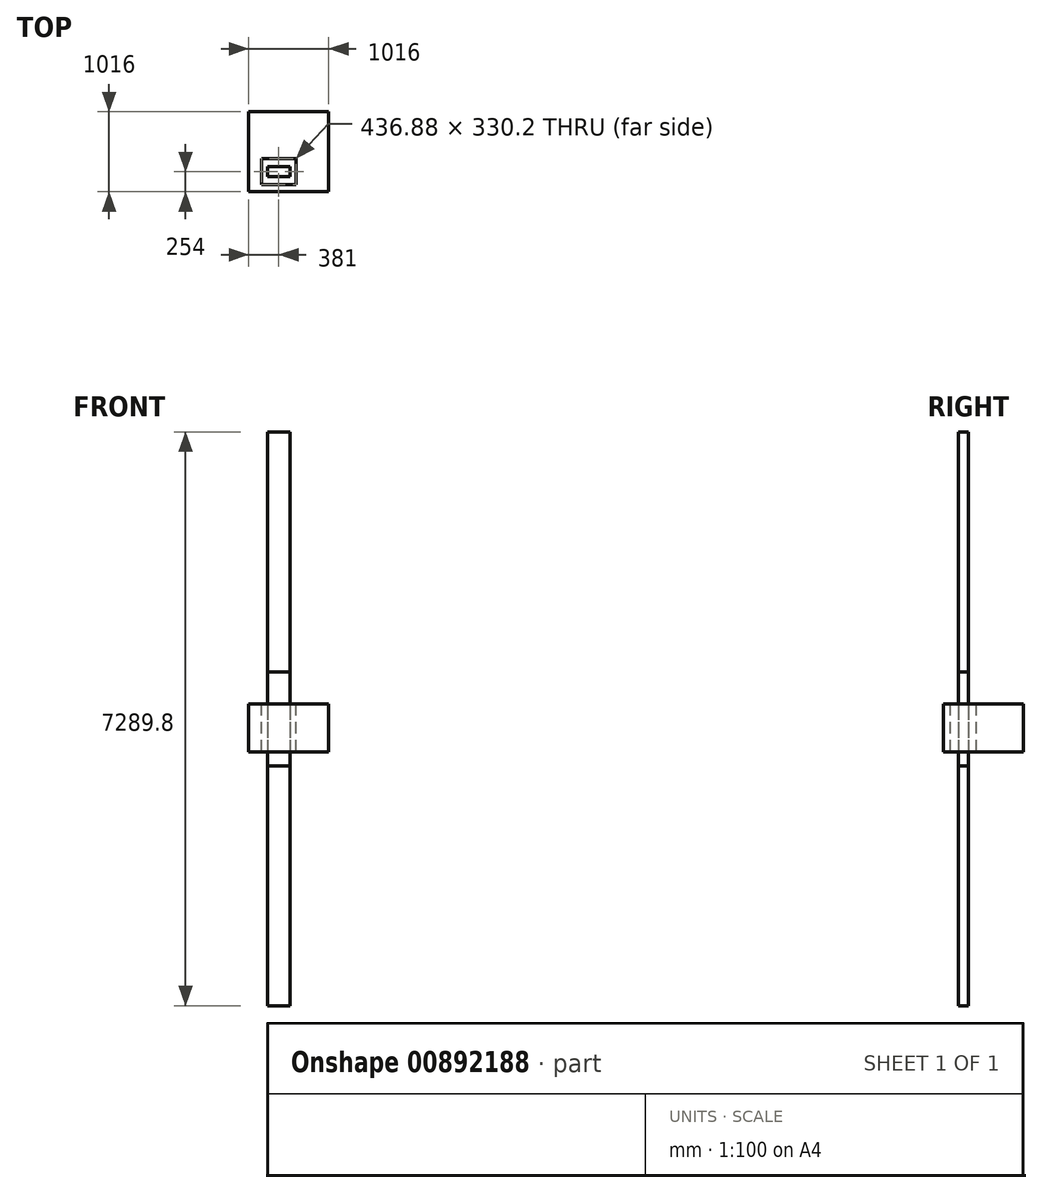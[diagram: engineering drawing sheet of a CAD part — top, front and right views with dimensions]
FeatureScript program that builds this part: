
annotation { "Feature Type Name" : "Feature", "Feature Type Description" : "" }
export const myFeature = defineFeature(function(context is Context, id is Id, definition is map)
    precondition{}
    {
        {
            var Q0;
            Q0=qCreatedBy(makeId("Top.planeOp"),FACE);
            var sketch = newSketch(context, id + "F0", { "sketchPlane" : qUnion([Q0])});
            skLineSegment(sketch, "E0.bottom", {"start": v(0, 0) * mm, "end": v(1016, 0) * mm});
            skLineSegment(sketch, "E0.top", {"start": v(0, 1016) * mm, "end": v(1016, 1016) * mm});
            skLineSegment(sketch, "E0.left", {"start": v(0, 0) * mm, "end": v(0, 1016) * mm});
            skLineSegment(sketch, "E0.right", {"start": v(1016, 0) * mm, "end": v(1016, 1016) * mm});
            skSolve(sketch);
        }
        {
            var Q0;
            Q0=makeQuery(id+"F0.imprint","IMPRINT",FACE,{"disambiguationData":[TD([[makeQuery(id+"F0.imprint","IMPRINT",EDGE,{"derivedFrom":sQuery(id+"F0.wireOp",EDGE,"E0.bottom")}),1.0]])]});
            extrude(context, id + "F1", {"entities" : qUnion([Q0]), "depth" : 609.6 * mm, "offsetDistance" : 25.4 * mm});
        }
        {
            var Q0;
            Q0=makeQuery(id+"F1.opExtrude","CAP_FACE",FACE,{"disambiguationData":[OSD([sQuery(id+"F0.wireOp",EDGE,"E0.bottom"),sQuery(id+"F0.wireOp",EDGE,"E0.top"),sQuery(id+"F0.wireOp",EDGE,"E0.left"),sQuery(id+"F0.wireOp",EDGE,"E0.right")])],"isStart":false});
            var sketch = newSketch(context, id + "F2", { "sketchPlane" : qUnion([Q0])});
            skLineSegment(sketch, "E1.bottom", {"start": v(0, 0) * mm, "end": v(381, 0) * mm, "construction": true});
            skLineSegment(sketch, "E1.top", {"start": v(0, 254) * mm, "end": v(381, 254) * mm, "construction": true});
            skLineSegment(sketch, "E1.left", {"start": v(0, 0) * mm, "end": v(0, 254) * mm, "construction": true});
            skLineSegment(sketch, "E1.right", {"start": v(381, 0) * mm, "end": v(381, 254) * mm, "construction": true});
            skLineSegment(sketch, "E2.bottom", {"start": v(523.24, 317.5) * mm, "end": v(238.76, 317.5) * mm});
            skLineSegment(sketch, "E2.top", {"start": v(523.24, 190.5) * mm, "end": v(238.76, 190.5) * mm});
            skLineSegment(sketch, "E2.left", {"start": v(523.24, 317.5) * mm, "end": v(523.24, 190.5) * mm});
            skLineSegment(sketch, "E2.right", {"start": v(238.76, 317.5) * mm, "end": v(238.76, 190.5) * mm});
            skPoint(sketch, "E2.middle", {"position": v(381, 254) * mm});
            skLineSegment(sketch, "E3.bottom", {"start": v(599.44, 419.1) * mm, "end": v(162.56, 419.1) * mm});
            skLineSegment(sketch, "E3.top", {"start": v(599.44, 88.9) * mm, "end": v(162.56, 88.9) * mm});
            skLineSegment(sketch, "E3.left", {"start": v(599.44, 419.1) * mm, "end": v(599.44, 88.9) * mm});
            skLineSegment(sketch, "E3.right", {"start": v(162.56, 419.1) * mm, "end": v(162.56, 88.9) * mm});
            skSolve(sketch);
        }
        {
            var Q0;
            Q0=makeQuery(id+"F2.imprint","IMPRINT",FACE,{"disambiguationData":[TD([[makeQuery(id+"F2.imprint","IMPRINT",EDGE,{"derivedFrom":sQuery(id+"F2.wireOp",EDGE,"E2.bottom")}),-1.0]])]});
            var Q1;
            Q1=makeQuery(id+"F2.imprint","IMPRINT",FACE,{"disambiguationData":[TD([[makeQuery(id+"F2.imprint","IMPRINT",EDGE,{"derivedFrom":sQuery(id+"F2.wireOp",EDGE,"E2.bottom")}),1.0]])]});
            extrude(context, id + "F3", {"entities" : qUnion([Q0, Q1]), "operationType" : NewBodyOperationType.REMOVE, "endBound" : BoundingType.THROUGH_ALL, "oppositeDirection" : true, "depth" : 25.4 * mm, "offsetDistance" : 25.4 * mm});
        }
        {
            var Q0;
            Q0=makeQuery(id+"F2.imprint","IMPRINT",FACE,{"disambiguationData":[TD([[makeQuery(id+"F2.imprint","IMPRINT",EDGE,{"derivedFrom":sQuery(id+"F2.wireOp",EDGE,"E2.bottom")}),1.0]])]});
            extrude(context, id + "F4", {"entities" : qUnion([Q0]), "endBound" : BoundingType.SYMMETRIC, "depth" : 1524 * mm, "offsetDistance" : 25.4 * mm});
        }
        {
            var Q0;
            Q0=makeQuery(id+"F4.opExtrude","CAP_FACE",FACE,{"disambiguationData":[OSD([sQuery(id+"F2.wireOp",EDGE,"E2.bottom"),sQuery(id+"F2.wireOp",EDGE,"E2.top"),sQuery(id+"F2.wireOp",EDGE,"E2.left"),sQuery(id+"F2.wireOp",EDGE,"E2.right")])],"isStart":true});
            extrude(context, id + "F5", {"entities" : qUnion([Q0]), "operationType" : NewBodyOperationType.ADD, "depth" : 1168.4 * mm, "offsetDistance" : 25.4 * mm});
        }
        {
            var Q0;
            Q0=makeQuery(id+"F4.opExtrude","CAP_FACE",FACE,{"disambiguationData":[OSD([sQuery(id+"F2.wireOp",EDGE,"E2.bottom"),sQuery(id+"F2.wireOp",EDGE,"E2.top"),sQuery(id+"F2.wireOp",EDGE,"E2.left"),sQuery(id+"F2.wireOp",EDGE,"E2.right")])],"isStart":false});
            extrude(context, id + "F6", {"entities" : qUnion([Q0]), "operationType" : NewBodyOperationType.ADD, "depth" : 431.8 * mm, "offsetDistance" : 25.4 * mm});
        }
        {
            var Q0;
            Q0=makeQuery(id+"F6.opExtrude","CAP_FACE",FACE,{"disambiguationData":[OSD([sQuery(id+"F2.wireOp",EDGE,"E2.bottom"),sQuery(id+"F2.wireOp",EDGE,"E2.top"),sQuery(id+"F2.wireOp",EDGE,"E2.left"),sQuery(id+"F2.wireOp",EDGE,"E2.right")])],"isStart":false});
            var Q1;
            Q1=makeQuery(id+"F1.opExtrude","CAP_FACE",FACE,{"disambiguationData":[OSD([sQuery(id+"F0.wireOp",EDGE,"E0.bottom"),sQuery(id+"F0.wireOp",EDGE,"E0.top"),sQuery(id+"F0.wireOp",EDGE,"E0.left"),sQuery(id+"F0.wireOp",EDGE,"E0.right")])],"isStart":false});
            extrude(context, id + "F7", {"entities" : qUnion([Q0]), "operationType" : NewBodyOperationType.REMOVE, "endBound" : BoundingType.UP_TO_SURFACE, "oppositeDirection" : true, "depth" : 25.4 * mm, "endBoundEntityFace" : qUnion([Q1]), "offsetDistance" : 25.4 * mm});
        }
        {
            var Q0;
            Q0=makeQuery(id+"F7.boolean.opBoolean","COPY",FACE,{"derivedFrom":makeQuery(id+"F7.opExtrude","CAP_FACE",FACE,{"disambiguationData":[OSD([sQuery(id+"F2.wireOp",EDGE,"E2.bottom"),sQuery(id+"F2.wireOp",EDGE,"E2.top"),sQuery(id+"F2.wireOp",EDGE,"E2.left"),sQuery(id+"F2.wireOp",EDGE,"E2.right")])],"isStart":false})});
            extrude(context, id + "F8", {"entities" : qUnion([Q0]), "operationType" : NewBodyOperationType.ADD, "depth" : 406.4 * mm, "offsetDistance" : 25.4 * mm});
        }
        {
            var Q0;
            Q0=makeQuery(id+"F5.opExtrude","CAP_FACE",FACE,{"disambiguationData":[OSD([sQuery(id+"F2.wireOp",EDGE,"E2.bottom"),sQuery(id+"F2.wireOp",EDGE,"E2.top"),sQuery(id+"F2.wireOp",EDGE,"E2.left"),sQuery(id+"F2.wireOp",EDGE,"E2.right")])],"isStart":false});
            var Q1;
            Q1=makeQuery(id+"F1.opExtrude","CAP_FACE",FACE,{"disambiguationData":[OSD([sQuery(id+"F0.wireOp",EDGE,"E0.bottom"),sQuery(id+"F0.wireOp",EDGE,"E0.top"),sQuery(id+"F0.wireOp",EDGE,"E0.left"),sQuery(id+"F0.wireOp",EDGE,"E0.right")])],"isStart":true});
            extrude(context, id + "F9", {"entities" : qUnion([Q0]), "operationType" : NewBodyOperationType.REMOVE, "endBound" : BoundingType.UP_TO_SURFACE, "oppositeDirection" : true, "depth" : 25.4 * mm, "endBoundEntityFace" : qUnion([Q1]), "offsetDistance" : 25.4 * mm});
        }
        {
            var Q0;
            Q0=makeQuery(id+"F9.boolean.opBoolean","COPY",FACE,{"derivedFrom":makeQuery(id+"F9.opExtrude","CAP_FACE",FACE,{"disambiguationData":[OSD([sQuery(id+"F2.wireOp",EDGE,"E2.bottom"),sQuery(id+"F2.wireOp",EDGE,"E2.top"),sQuery(id+"F2.wireOp",EDGE,"E2.left"),sQuery(id+"F2.wireOp",EDGE,"E2.right")])],"isStart":false})});
            extrude(context, id + "F10", {"entities" : qUnion([Q0]), "operationType" : NewBodyOperationType.ADD, "depth" : 177.8 * mm, "offsetDistance" : 25.4 * mm});
        }
        {
            var Q0;
            Q0=makeQuery(id+"F8.opExtrude","CAP_FACE",FACE,{"disambiguationData":[OSD([sQuery(id+"F2.wireOp",EDGE,"E2.bottom"),sQuery(id+"F2.wireOp",EDGE,"E2.top"),sQuery(id+"F2.wireOp",EDGE,"E2.left"),sQuery(id+"F2.wireOp",EDGE,"E2.right")])],"isStart":false});
            extrude(context, id + "F11", {"entities" : qUnion([Q0]), "depth" : 3048 * mm, "offsetDistance" : 25.4 * mm});
        }
        {
            var Q0;
            Q0=makeQuery(id+"F10.opExtrude","CAP_FACE",FACE,{"disambiguationData":[OSD([sQuery(id+"F2.wireOp",EDGE,"E2.bottom"),sQuery(id+"F2.wireOp",EDGE,"E2.top"),sQuery(id+"F2.wireOp",EDGE,"E2.left"),sQuery(id+"F2.wireOp",EDGE,"E2.right")])],"isStart":false});
            extrude(context, id + "F12", {"entities" : qUnion([Q0]), "depth" : 3048 * mm, "offsetDistance" : 25.4 * mm});
        }
    });
